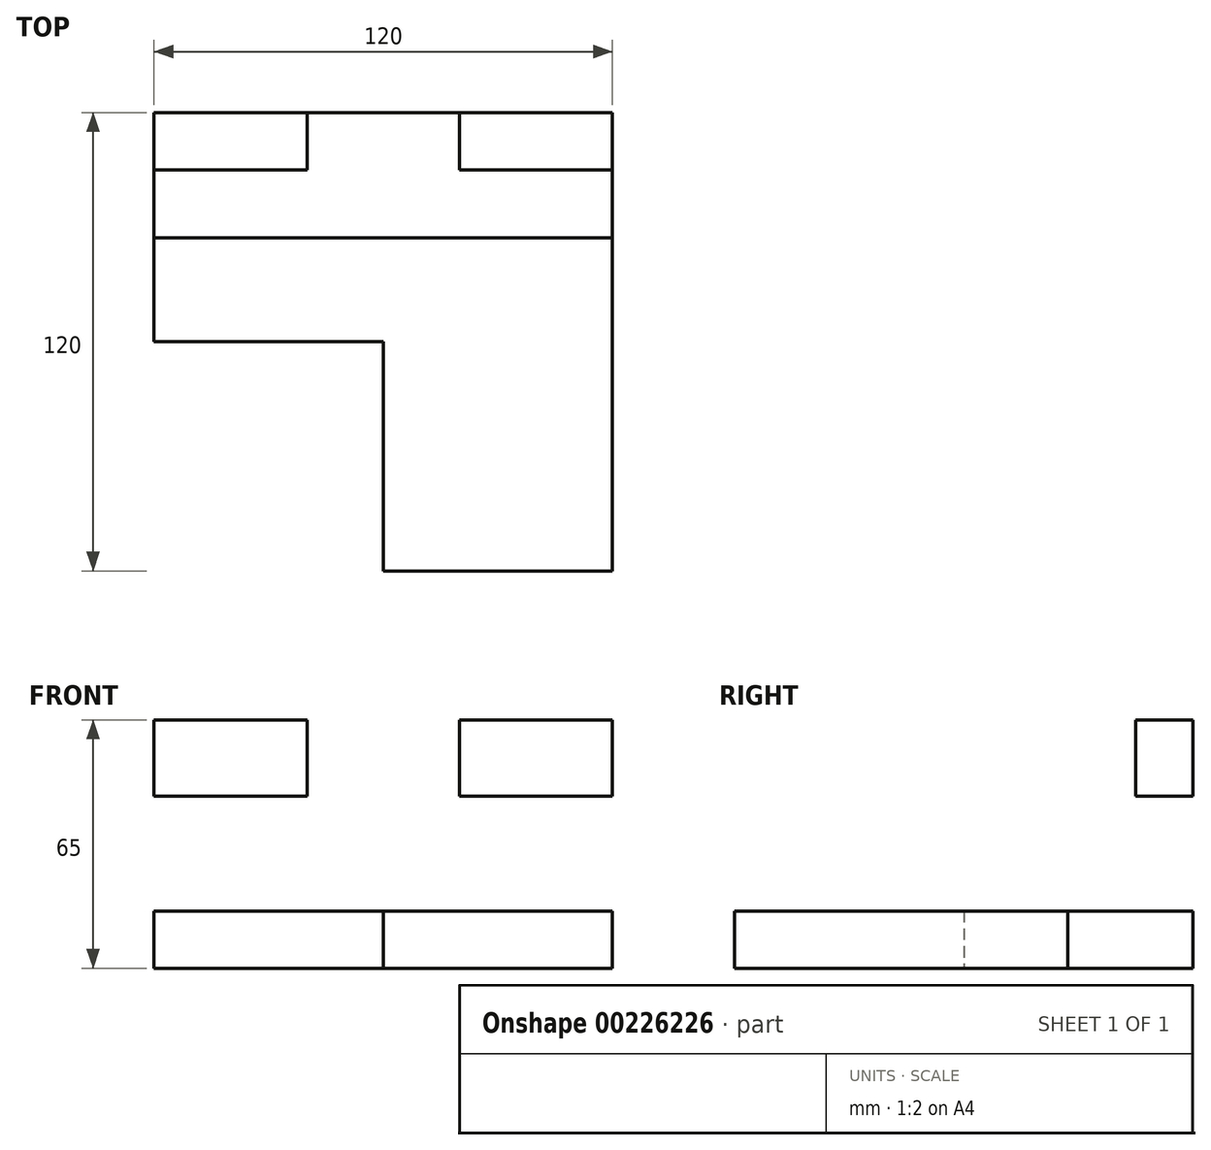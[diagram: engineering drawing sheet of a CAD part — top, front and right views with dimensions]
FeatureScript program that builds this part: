
annotation { "Feature Type Name" : "Feature", "Feature Type Description" : "" }
export const myFeature = defineFeature(function(context is Context, id is Id, definition is map)
    precondition{}
    {
        {
            var Q0;
            Q0=qCreatedBy(makeId("Top.planeOp"),FACE);
            var sketch = newSketch(context, id + "F0", { "sketchPlane" : qUnion([Q0])});
            skLineSegment(sketch, "E0.bottom", {"start": v(0, 0) * mm, "end": v(-120, 0) * mm});
            skLineSegment(sketch, "E0.top", {"start": v(0, -120) * mm, "end": v(-120, -120) * mm});
            skLineSegment(sketch, "E0.left", {"start": v(0, 0) * mm, "end": v(0, -120) * mm});
            skLineSegment(sketch, "E0.right", {"start": v(-120, 0) * mm, "end": v(-120, -120) * mm});
            skLineSegment(sketch, "E1.bottom", {"start": v(-120, -120) * mm, "end": v(-60, -120) * mm});
            skLineSegment(sketch, "E1.top", {"start": v(-120, -60) * mm, "end": v(-60, -60) * mm});
            skLineSegment(sketch, "E1.left", {"start": v(-120, -120) * mm, "end": v(-120, -60) * mm});
            skLineSegment(sketch, "E1.right", {"start": v(-60, -120) * mm, "end": v(-60, -60) * mm});
            skSolve(sketch);
        }
        {
            var Q0;
            Q0=makeQuery(id+"F0.imprint","IMPRINT",FACE,{"disambiguationData":[TD([[makeQuery(id+"F0.imprint","IMPRINT",EDGE,{"derivedFrom":sQuery(id+"F0.wireOp",EDGE,"E0.bottom")}),1.0]])]});
            extrude(context, id + "F1", {"entities" : qUnion([Q0]), "depth" : 15 * mm});
        }
        {
            var Q0;
            Q0=makeQuery(id+"F1.opExtrude","SWEPT_FACE",FACE,{"disambiguationData":[OSD([sQuery(id+"F0.wireOp",EDGE,"E0.bottom")])]});
            var sketch = newSketch(context, id + "F2", { "sketchPlane" : qUnion([Q0])});
            skLineSegment(sketch, "E2.bottom", {"start": v(0, 0) * mm, "end": v(120, 0) * mm});
            skLineSegment(sketch, "E2.top", {"start": v(0, 65) * mm, "end": v(120, 65) * mm});
            skLineSegment(sketch, "E2.left", {"start": v(0, 0) * mm, "end": v(0, 65) * mm});
            skLineSegment(sketch, "E2.right", {"start": v(120, 0) * mm, "end": v(120, 65) * mm});
            skLineSegment(sketch, "E3.bottom", {"start": v(0, 65) * mm, "end": v(40, 65) * mm});
            skLineSegment(sketch, "E3.top", {"start": v(0, 45) * mm, "end": v(40, 45) * mm});
            skLineSegment(sketch, "E3.left", {"start": v(0, 65) * mm, "end": v(0, 45) * mm});
            skLineSegment(sketch, "E3.right", {"start": v(40, 65) * mm, "end": v(40, 45) * mm});
            skLineSegment(sketch, "E4.bottom", {"start": v(120, 65) * mm, "end": v(80, 65) * mm});
            skLineSegment(sketch, "E4.top", {"start": v(120, 45) * mm, "end": v(80, 45) * mm});
            skLineSegment(sketch, "E4.left", {"start": v(120, 65) * mm, "end": v(120, 45) * mm});
            skLineSegment(sketch, "E4.right", {"start": v(80, 65) * mm, "end": v(80, 45) * mm});
            skSolve(sketch);
        }
        {
            var Q0;
            Q0=makeQuery(id+"F2.imprint","IMPRINT",FACE,{"disambiguationData":[TD([[makeQuery(id+"F2.imprint","IMPRINT",EDGE,{"derivedFrom":sQuery(id+"F2.wireOp",EDGE,"E2.top")}),-1.0]])]});
            extrude(context, id + "F3", {"entities" : qUnion([Q0]), "operationType" : NewBodyOperationType.ADD, "oppositeDirection" : true, "depth" : 15 * mm});
        }
        {
            var Q0;
            {var subQ0=sQuery(id+"F0.wireOp",EDGE,"E0.bottom");Q0=makeQuery(id+"F3.boolean.opBoolean","MERGE",FACE,{"derivedFrom":[makeQuery(id+"F1.opExtrude","SWEPT_FACE",FACE,{"disambiguationData":[OSD([subQ0])]}),makeQuery(id+"F3.opExtrude","CAP_FACE",FACE,{"disambiguationData":[OSD([subQ0,sQuery(id+"F2.wireOp",EDGE,"E2.top"),sQuery(id+"F2.wireOp",EDGE,"E2.left"),sQuery(id+"F2.wireOp",EDGE,"E2.right"),sQuery(id+"F2.wireOp",EDGE,"E3.top"),sQuery(id+"F2.wireOp",EDGE,"E3.right"),sQuery(id+"F2.wireOp",EDGE,"E4.top"),sQuery(id+"F2.wireOp",EDGE,"E4.right")])],"isStart":true})]});}
            var sketch = newSketch(context, id + "F4", { "sketchPlane" : qUnion([Q0])});
            skLineSegment(sketch, "E5.bottom", {"start": v(0, 0) * mm, "end": v(120, 0) * mm});
            skLineSegment(sketch, "E5.top", {"start": v(0, 65) * mm, "end": v(120, 65) * mm});
            skLineSegment(sketch, "E5.left", {"start": v(0, 0) * mm, "end": v(0, 65) * mm});
            skLineSegment(sketch, "E5.right", {"start": v(120, 0) * mm, "end": v(120, 65) * mm});
            skSolve(sketch);
        }
        {
            var Q0;
            {var subQ1=sQuery(id+"F4.wireOp",EDGE,"E5.bottom");Q0=makeQuery(id+"F4.imprint","IMPRINT",FACE,{"disambiguationData":[TD([[makeQuery(id+"F4.imprint","IMPRINT",EDGE,{"derivedFrom":subQ1}),1.0]])]});}
            extrude(context, id + "F5", {"entities" : qUnion([Q0]), "oppositeDirection" : true, "depth" : 32.8 * mm});
        }
    });
